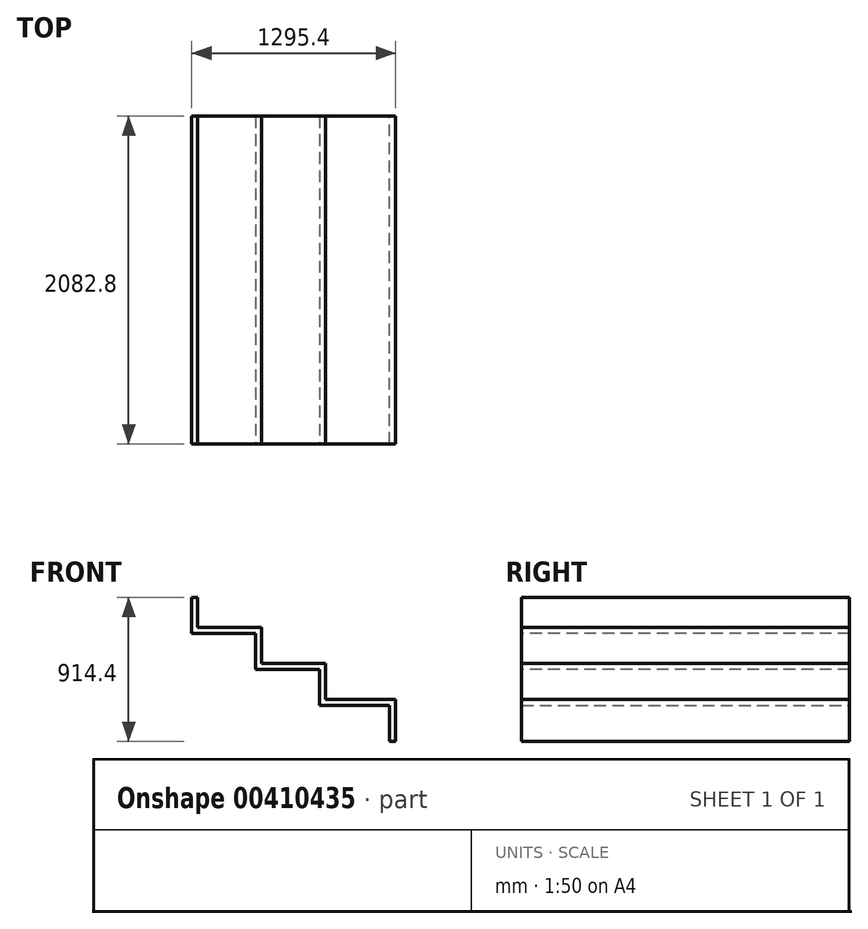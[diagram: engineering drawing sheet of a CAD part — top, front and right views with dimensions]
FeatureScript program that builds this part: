
annotation { "Feature Type Name" : "Feature", "Feature Type Description" : "" }
export const myFeature = defineFeature(function(context is Context, id is Id, definition is map)
    precondition{}
    {
        {
            var Q0;
            Q0=qCreatedBy(makeId("Right.planeOp"),FACE);
            var sketch = newSketch(context, id + "F0", { "sketchPlane" : qUnion([Q0])});
            skLineSegment(sketch, "E0.bottom", {"start": v(-1041.4, 114.3) * mm, "end": v(1041.4, 114.3) * mm});
            skLineSegment(sketch, "E0.top", {"start": v(-1041.4, -114.3) * mm, "end": v(1041.4, -114.3) * mm});
            skLineSegment(sketch, "E0.left", {"start": v(-1041.4, 114.3) * mm, "end": v(-1041.4, -114.3) * mm});
            skLineSegment(sketch, "E0.right", {"start": v(1041.4, 114.3) * mm, "end": v(1041.4, -114.3) * mm});
            skPoint(sketch, "E0.middle", {"position": v(0, 0) * mm});
            skLineSegment(sketch, "E1.top", {"start": v(-1041.4, -76.2) * mm, "end": v(1041.4, -76.2) * mm});
            skLineSegment(sketch, "E1.left", {"start": v(-1041.4, -114.3) * mm, "end": v(-1041.4, -76.2) * mm});
            skLineSegment(sketch, "E1.right", {"start": v(1041.4, -114.3) * mm, "end": v(1041.4, -76.2) * mm});
            skSolve(sketch);
        }
        {
            var Q0;
            Q0 = qSketchRegion(id + "F0", true);
            extrude(context, id + "F1", {"entities" : qUnion([Q0]), "depth" : 38.1 * mm, "offsetDistance" : 25.4 * mm});
        }
        {
            var Q0;
            Q0=makeQuery(id+"F0.imprint","IMPRINT",FACE,{"disambiguationData":[TD([[makeQuery(id+"F0.imprint","IMPRINT",EDGE,{"derivedFrom":sQuery(id+"F0.wireOp",EDGE,"E0.top")}),1.0]])]});
            extrude(context, id + "F2", {"entities" : qUnion([Q0]), "operationType" : NewBodyOperationType.ADD, "depth" : 444.5 * mm, "offsetDistance" : 25.4 * mm});
        }
        {
            var Q0;
            Q0=makeQuery(id+"F2.opExtrude","SWEPT_FACE",FACE,{"disambiguationData":[OSD([sQuery(id+"F0.wireOp",EDGE,"E1.top")])]});
            var sketch = newSketch(context, id + "F3", { "sketchPlane" : qUnion([Q0])});
            skLineSegment(sketch, "E2.bottom", {"start": v(444.5, 1041.4) * mm, "end": v(406.4, 1041.4) * mm});
            skLineSegment(sketch, "E2.top", {"start": v(444.5, -1041.4) * mm, "end": v(406.4, -1041.4) * mm});
            skLineSegment(sketch, "E2.left", {"start": v(444.5, 1041.4) * mm, "end": v(444.5, -1041.4) * mm});
            skLineSegment(sketch, "E2.right", {"start": v(406.4, 1041.4) * mm, "end": v(406.4, -1041.4) * mm});
            skSolve(sketch);
        }
        {
            var Q0;
            Q0 = qSketchRegion(id + "F3", true);
            extrude(context, id + "F4", {"entities" : qUnion([Q0]), "operationType" : NewBodyOperationType.ADD, "oppositeDirection" : true, "depth" : 266.7 * mm, "offsetDistance" : 25.4 * mm});
        }
        {
            var Q0;
            Q0=makeQuery(id+"F4.opExtrude","SWEPT_FACE",FACE,{"disambiguationData":[OSD([sQuery(id+"F3.wireOp",EDGE,"E2.right")])]});
            var sketch = newSketch(context, id + "F5", { "sketchPlane" : qUnion([Q0])});
            skLineSegment(sketch, "E3.bottom", {"start": v(-1041.4, -342.9) * mm, "end": v(1041.4, -342.9) * mm});
            skLineSegment(sketch, "E3.top", {"start": v(-1041.4, -304.8) * mm, "end": v(1041.4, -304.8) * mm});
            skLineSegment(sketch, "E3.left", {"start": v(-1041.4, -342.9) * mm, "end": v(-1041.4, -304.8) * mm});
            skLineSegment(sketch, "E3.right", {"start": v(1041.4, -342.9) * mm, "end": v(1041.4, -304.8) * mm});
            skSolve(sketch);
        }
        {
            var Q0;
            Q0 = qSketchRegion(id + "F5", true);
            extrude(context, id + "F6", {"entities" : qUnion([Q0]), "operationType" : NewBodyOperationType.ADD, "oppositeDirection" : true, "depth" : 444.5 * mm, "offsetDistance" : 25.4 * mm});
        }
        {
            var Q0;
            Q0=makeQuery(id+"F6.opExtrude","SWEPT_FACE",FACE,{"disambiguationData":[OSD([sQuery(id+"F5.wireOp",EDGE,"E3.top")])]});
            var sketch = newSketch(context, id + "F7", { "sketchPlane" : qUnion([Q0])});
            skLineSegment(sketch, "E4.bottom", {"start": v(850.9, 1041.4) * mm, "end": v(812.8, 1041.4) * mm});
            skLineSegment(sketch, "E4.top", {"start": v(850.9, -1041.4) * mm, "end": v(812.8, -1041.4) * mm});
            skLineSegment(sketch, "E4.left", {"start": v(850.9, 1041.4) * mm, "end": v(850.9, -1041.4) * mm});
            skLineSegment(sketch, "E4.right", {"start": v(812.8, 1041.4) * mm, "end": v(812.8, -1041.4) * mm});
            skSolve(sketch);
        }
        {
            var Q0;
            Q0 = qSketchRegion(id + "F7", true);
            extrude(context, id + "F8", {"entities" : qUnion([Q0]), "operationType" : NewBodyOperationType.ADD, "oppositeDirection" : true, "depth" : 266.7 * mm, "offsetDistance" : 25.4 * mm});
        }
        {
            var Q0;
            Q0=makeQuery(id+"F8.opExtrude","SWEPT_FACE",FACE,{"disambiguationData":[OSD([sQuery(id+"F7.wireOp",EDGE,"E4.right")])]});
            var sketch = newSketch(context, id + "F9", { "sketchPlane" : qUnion([Q0])});
            skLineSegment(sketch, "E5.bottom", {"start": v(-1041.4, -571.5) * mm, "end": v(1041.4, -571.5) * mm});
            skLineSegment(sketch, "E5.top", {"start": v(-1041.4, -533.4) * mm, "end": v(1041.4, -533.4) * mm});
            skLineSegment(sketch, "E5.left", {"start": v(-1041.4, -571.5) * mm, "end": v(-1041.4, -533.4) * mm});
            skLineSegment(sketch, "E5.right", {"start": v(1041.4, -571.5) * mm, "end": v(1041.4, -533.4) * mm});
            skSolve(sketch);
        }
        {
            var Q0;
            Q0 = qSketchRegion(id + "F9", true);
            extrude(context, id + "F10", {"entities" : qUnion([Q0]), "operationType" : NewBodyOperationType.ADD, "oppositeDirection" : true, "depth" : 482.6 * mm, "offsetDistance" : 25.4 * mm});
        }
        {
            var Q0;
            Q0=makeQuery(id+"F10.opExtrude","SWEPT_FACE",FACE,{"disambiguationData":[OSD([sQuery(id+"F9.wireOp",EDGE,"E5.top")])]});
            var sketch = newSketch(context, id + "F11", { "sketchPlane" : qUnion([Q0])});
            skLineSegment(sketch, "E6.bottom", {"start": v(1295.4, -1041.4) * mm, "end": v(1257.3, -1041.4) * mm});
            skLineSegment(sketch, "E6.top", {"start": v(1295.4, 1041.4) * mm, "end": v(1257.3, 1041.4) * mm});
            skLineSegment(sketch, "E6.left", {"start": v(1295.4, -1041.4) * mm, "end": v(1295.4, 1041.4) * mm});
            skLineSegment(sketch, "E6.right", {"start": v(1257.3, -1041.4) * mm, "end": v(1257.3, 1041.4) * mm});
            skSolve(sketch);
        }
        {
            var Q0;
            Q0 = qSketchRegion(id + "F11", true);
            extrude(context, id + "F12", {"entities" : qUnion([Q0]), "operationType" : NewBodyOperationType.ADD, "oppositeDirection" : true, "depth" : 266.7 * mm, "offsetDistance" : 25.4 * mm});
        }
    });
